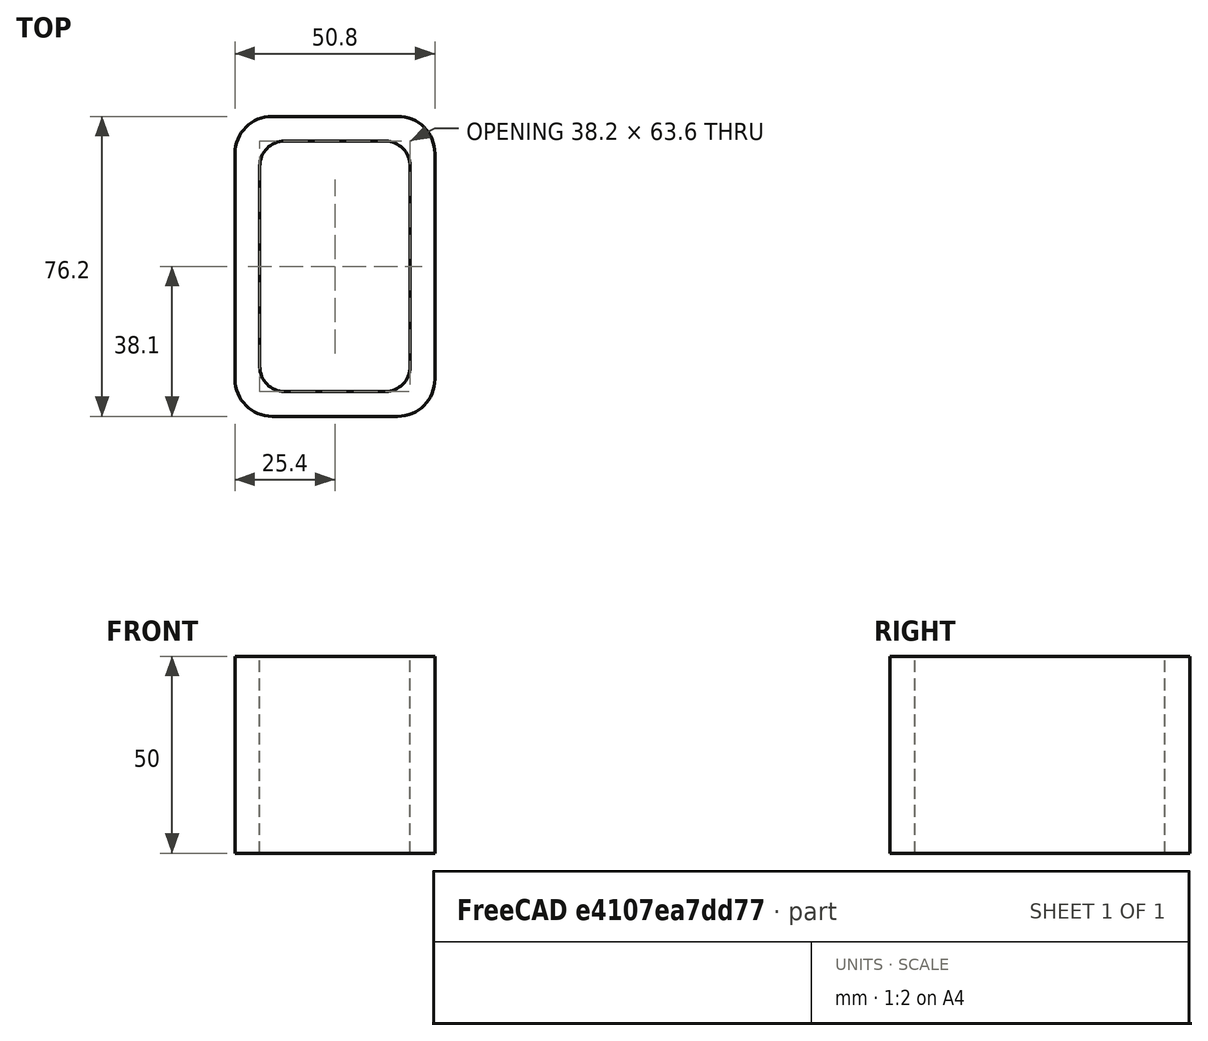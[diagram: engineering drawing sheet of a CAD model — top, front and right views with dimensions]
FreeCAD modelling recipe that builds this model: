
FCSTD DOCUMENT  (FreeCAD 0.15R4671 (Git))
Label: Rectangular hollow section 76.2 x50.8 x6.3 EN10219 S235JRH
License: All rights reserved
LicenseURL: http://en.wikipedia.org/wiki/All_rights_reserved
objects: Sketcher::SketchObject×1, Part::Extrusion×1
note: 2 computed .brp shape members not serialized (recipe doc carries the construction recipe); baked Part::Feature solids carry a one-line shape summary decoded from their .brp

FEATURE [Sketcher::SketchObject] Sketch
  sketch-geometry (16):
    g0: LineSegment StartX=-12.8 StartY=31.8 StartZ=0 EndX=12.8 EndY=31.8 EndZ=0
    g1: LineSegment StartX=19.1 StartY=25.5 StartZ=0 EndX=19.1 EndY=-25.5 EndZ=0
    g2: LineSegment StartX=12.8 StartY=-31.8 StartZ=0 EndX=-12.8 EndY=-31.8 EndZ=0
    g3: LineSegment StartX=-19.1 StartY=-25.5 StartZ=0 EndX=-19.1 EndY=25.5 EndZ=0
    g4: LineSegment StartX=-15.95 StartY=38.1 StartZ=0 EndX=15.95 EndY=38.1 EndZ=0
    g5: LineSegment StartX=25.4 StartY=28.65 StartZ=0 EndX=25.4 EndY=-28.65 EndZ=0
    g6: LineSegment StartX=15.95 StartY=-38.1 StartZ=0 EndX=-15.95 EndY=-38.1 EndZ=0
    g7: LineSegment StartX=-25.4 StartY=-28.65 StartZ=0 EndX=-25.4 EndY=28.65 EndZ=0
    g8: ArcOfCircle CenterX=-12.8 CenterY=25.5 CenterZ=0 NormalX=0 NormalY=0 NormalZ=1 Radius=6.3 StartAngle=1.5708 EndAngle=3.14159
    g9: ArcOfCircle CenterX=12.8 CenterY=25.5 CenterZ=0 NormalX=0 NormalY=0 NormalZ=1 Radius=6.3 StartAngle=0 EndAngle=1.5708
    g10: ArcOfCircle CenterX=12.8 CenterY=-25.5 CenterZ=0 NormalX=0 NormalY=0 NormalZ=1 Radius=6.3 StartAngle=4.71239 EndAngle=6.28319
    g11: ArcOfCircle CenterX=-12.8 CenterY=-25.5 CenterZ=0 NormalX=0 NormalY=0 NormalZ=1 Radius=6.3 StartAngle=3.14159 EndAngle=4.71239
    g12: ArcOfCircle CenterX=15.95 CenterY=28.65 CenterZ=0 NormalX=0 NormalY=0 NormalZ=1 Radius=9.45 StartAngle=0 EndAngle=1.5708
    g13: ArcOfCircle CenterX=15.95 CenterY=-28.65 CenterZ=0 NormalX=0 NormalY=0 NormalZ=1 Radius=9.45 StartAngle=4.71239 EndAngle=6.28319
    g14: ArcOfCircle CenterX=-15.95 CenterY=-28.65 CenterZ=0 NormalX=0 NormalY=0 NormalZ=1 Radius=9.45 StartAngle=3.14159 EndAngle=4.71239
    g15: ArcOfCircle CenterX=-15.95 CenterY=28.65 CenterZ=0 NormalX=0 NormalY=0 NormalZ=1 Radius=9.45 StartAngle=1.5708 EndAngle=3.14159
  constraints (36):
    c: Horizontal(g2)
    c: Vertical(g3)
    c: Horizontal(g6)
    c: Vertical(g7)
    c: Tangent(g3,g8) = 1.5708
    c: Tangent(g0,g8) = 1.5708
    c: Tangent(g0,g9) = 1.5708
    c: Tangent(g1,g9) = 1.5708
    c: Tangent(g1,g10) = 1.5708
    c: Tangent(g2,g10) = 1.5708
    c: Tangent(g2,g11) = 1.5708
    c: Tangent(g3,g11) = 1.5708
    c: Tangent(g4,g12) = 1.5708
    c: Tangent(g5,g12) = 1.5708
    c: Tangent(g5,g13) = 1.5708
    c: Tangent(g6,g13) = 1.5708
    c: Tangent(g6,g14) = 1.5708
    c: Tangent(g7,g14) = 1.5708
    c: Tangent(g7,g15) = 1.5708
    c: Tangent(g4,g15) = 1.5708
    c: Equal(g9,g8)
    c: Equal(g9,g11)
    c: Equal(g9,g10)
    c: Equal(g12,g15)
    c: Equal(g12,g14)
    c: Equal(g12,g13)
    c: Symmetric(g4,g6,g-1)
    c: Symmetric(g7,g5,g-2)
    c: DistanceY(g4,g6) = -76.2
    c: DistanceX(g7,g5) = 50.8
    c: Symmetric(g3,g1,g-2)
    c: Symmetric(g0,g2,g-1)
    c: DistanceY(g0,g4) = 6.3
    c: DistanceX(g5,g1) = -6.3
    c: Radius(g9) = 6.3
    c: Radius(g12) = 9.45
FEATURE [Part::Extrusion] Extrude  label="Rectangular hollow section 76.2 x50.8 x6.3 EN10219 S235JRH"
  Base = -> Sketch
  Dir = (0,0,50)
  Solid = true
